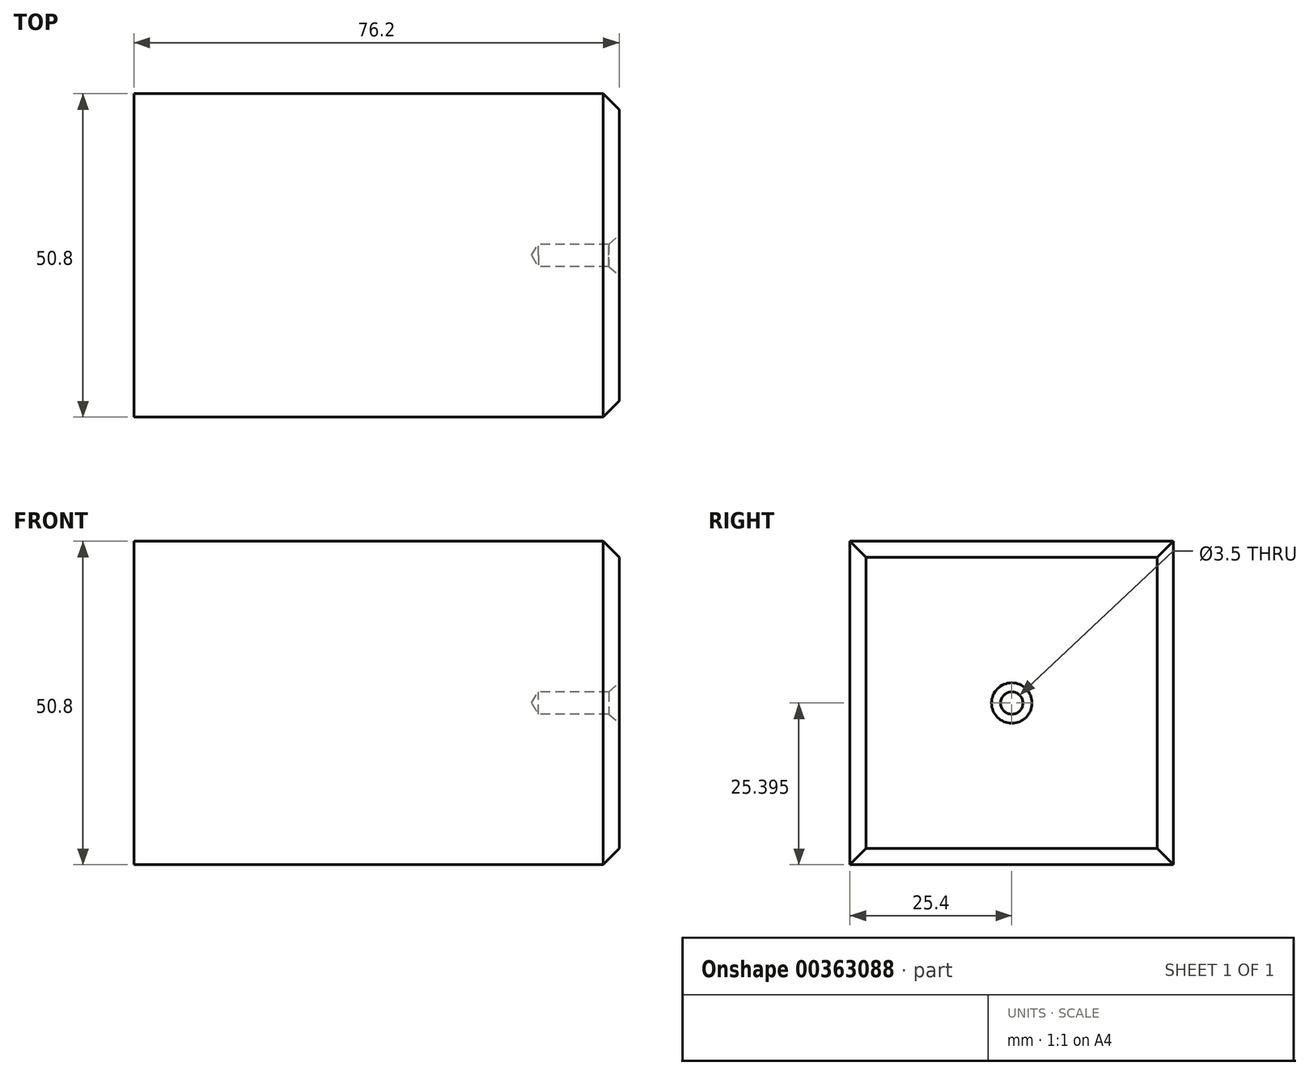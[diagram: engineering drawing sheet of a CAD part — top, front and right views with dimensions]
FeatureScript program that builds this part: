
annotation { "Feature Type Name" : "Feature", "Feature Type Description" : "" }
export const myFeature = defineFeature(function(context is Context, id is Id, definition is map)
    precondition{}
    {
        {
            var Q0;
            Q0=qCreatedBy(makeId("Front.planeOp"),FACE);
            var sketch = newSketch(context, id + "F0", { "sketchPlane" : qUnion([Q0])});
            skLineSegment(sketch, "E0.bottom", {"start": v(-47.9, 23.72) * mm, "end": v(28.3, 23.72) * mm});
            skLineSegment(sketch, "E0.top", {"start": v(-47.9, -27.08) * mm, "end": v(28.3, -27.08) * mm});
            skLineSegment(sketch, "E0.left", {"start": v(-47.9, 23.72) * mm, "end": v(-47.9, -27.08) * mm});
            skLineSegment(sketch, "E0.right", {"start": v(28.3, 23.72) * mm, "end": v(28.3, -27.08) * mm});
            skSolve(sketch);
        }
        {
            var Q0;
            Q0=makeQuery(id+"F0.imprint","IMPRINT",FACE,{"disambiguationData":[TD([[makeQuery(id+"F0.imprint","IMPRINT",EDGE,{"derivedFrom":sQuery(id+"F0.wireOp",EDGE,"E0.bottom")}),-1.0]])]});
            extrude(context, id + "F1", {"entities" : qUnion([Q0]), "depth" : 50.8 * mm, "symmetric" : true});
        }
        {
            var Q0;
            Q0=makeQuery(id+"F1.opExtrude","SWEPT_FACE",FACE,{"disambiguationData":[OSD([sQuery(id+"F0.wireOp",EDGE,"E0.right")])]});
            var sketch = newSketch(context, id + "F2", { "sketchPlane" : qUnion([Q0])});
            skLineSegment(sketch, "E1", {"start": v(25.4, -1.68) * mm, "end": v(-25.4, -1.68) * mm});
            skLineSegment(sketch, "E2", {"start": v(0, -1.68) * mm, "end": v(0, 23.72) * mm});
            skLineSegment(sketch, "E3", {"start": v(0, -1.68) * mm, "end": v(0, -27.08) * mm});
            skSolve(sketch);
        }
        {
            var Q0;
            Q0=sQuery(id+"F2.wireOp",VERTEX,"E3.start");
            var Q1;
            Q1=makeQuery(id+"F1.opExtrude","SWEPT_BODY",BODY,{"disambiguationData":[OSD([sQuery(id+"F0.wireOp",EDGE,"E0.bottom"),sQuery(id+"F0.wireOp",EDGE,"E0.top"),sQuery(id+"F0.wireOp",EDGE,"E0.left"),sQuery(id+"F0.wireOp",EDGE,"E0.right")])]});
            hole(context, id + "F3", {"style" : HoleStyle.C_SINK, "endStyle" : HoleEndStyle.BLIND, "standardTappedOrClearance" : lookupTablePath({ "standard" : "ISO", "size" : "3.5", "type" : "Drilled" }), "standardBlindInLast" : lookupTablePath({ "standard" : "ISO", "size" : "3.5", "type" : "Drilled" }), "holeDiameter" : 3.5 * mm, "cSinkDiameter" : 6.35 * mm, "cSinkAngle" : 82 * degree, "holeDepth" : 12.7 * mm, "isTappedThrough" : true, "tappedDepth" : 12.7 * mm, "tapClearance" : 3, "locations" : qUnion([Q0]), "scope" : qUnion([Q1]), "startStyle" : HoleStartStyle.SKETCH});
        }
        {
            var Q0;
            Q0=makeQuery(id+"F1.opExtrude","SWEPT_EDGE",EDGE,{"disambiguationData":[OSD([sQuery(id+"F0.wireOp",EDGE,"E0.top"),sQuery(id+"F0.wireOp",EDGE,"E0.right")])]});
            var Q1;
            Q1=makeQuery(id+"F1.opExtrude","CAP_EDGE",EDGE,{"disambiguationData":[OSD([sQuery(id+"F0.wireOp",EDGE,"E0.right")])],"isStart":false});
            var Q2;
            Q2=makeQuery(id+"F1.opExtrude","SWEPT_EDGE",EDGE,{"disambiguationData":[OSD([sQuery(id+"F0.wireOp",EDGE,"E0.bottom"),sQuery(id+"F0.wireOp",EDGE,"E0.right")])]});
            var Q3;
            Q3=makeQuery(id+"F1.opExtrude","CAP_EDGE",EDGE,{"disambiguationData":[OSD([sQuery(id+"F0.wireOp",EDGE,"E0.right")])],"isStart":true});
            chamfer(context, id + "F4", {"entities" : qUnion([Q0, Q1, Q2, Q3]), "width" : 2.54 * mm, "tangentPropagation" : true});
        }
    });
